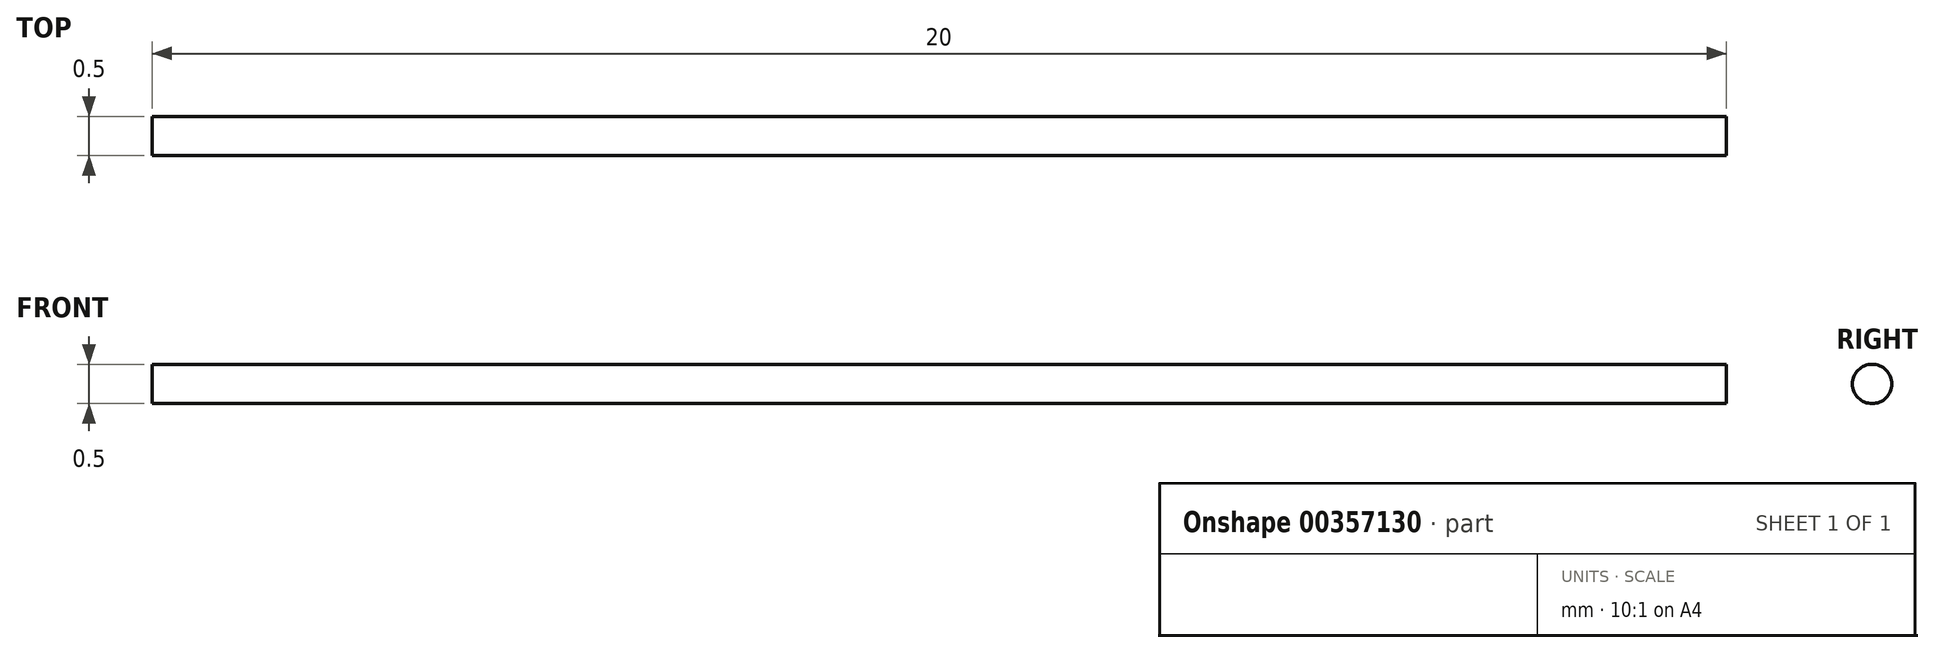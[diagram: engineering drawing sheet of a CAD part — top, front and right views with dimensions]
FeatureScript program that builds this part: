
annotation { "Feature Type Name" : "Feature", "Feature Type Description" : "" }
export const myFeature = defineFeature(function(context is Context, id is Id, definition is map)
    precondition{}
    {
        {
            var Q0;
            Q0=qCreatedBy(makeId("Right.planeOp"),FACE);
            var sketch = newSketch(context, id + "F0", { "sketchPlane" : qUnion([Q0])});
            skCircle(sketch, "E0", {"center": v(0, 0) * mm, "radius": 0.25 * mm});
            skSolve(sketch);
        }
        {
            var Q0;
            Q0 = qSketchRegion(id + "F0", true);
            extrude(context, id + "F1", {"entities" : qUnion([Q0]), "depth" : 20 * mm});
        }
    });
